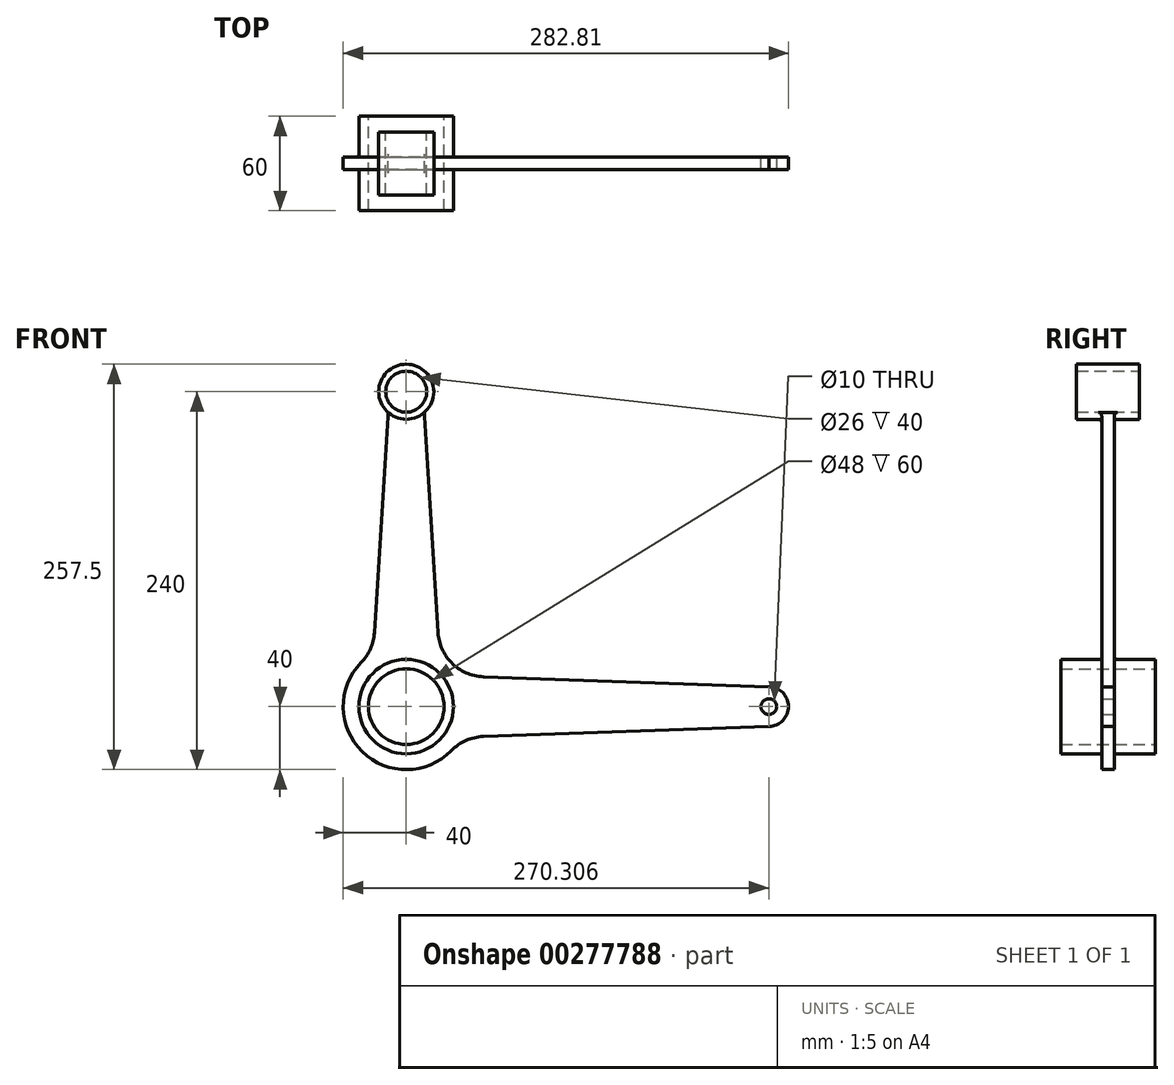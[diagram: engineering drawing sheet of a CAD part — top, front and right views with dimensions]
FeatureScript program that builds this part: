
annotation { "Feature Type Name" : "Feature", "Feature Type Description" : "" }
export const myFeature = defineFeature(function(context is Context, id is Id, definition is map)
    precondition{}
    {
        {
            var Q0;
            Q0=qCreatedBy(makeId("Front.planeOp"),FACE);
            var sketch = newSketch(context, id + "F0", { "sketchPlane" : qUnion([Q0])});
            skCircle(sketch, "E0", {"center": v(0, 0) * mm, "radius": 40 * mm});
            skCircle(sketch, "E1", {"center": v(0, 200) * mm, "radius": 17.5 * mm});
            skLineSegment(sketch, "E2", {"start": v(-11.5, 186.8) * mm, "end": v(-21, 34.04) * mm});
            skLineSegment(sketch, "E3.MirrorCS", {"start": v(11.5, 186.8) * mm, "end": v(21, 34.04) * mm});
            skCircle(sketch, "E4", {"center": v(230.3, 0) * mm, "radius": 12.5 * mm});
            skCircle(sketch, "E5", {"center": v(230.3, 0) * mm, "radius": 5 * mm});
            skLineSegment(sketch, "E6", {"start": v(34.92, 19.5) * mm, "end": v(230.3, 12.5) * mm});
            skLineSegment(sketch, "E7.MirrorCS", {"start": v(34.92, -19.5) * mm, "end": v(230.3, -12.5) * mm});
            skCircle(sketch, "E8", {"center": v(0, 0) * mm, "radius": 30 * mm});
            skCircle(sketch, "E9", {"center": v(0, 0) * mm, "radius": 24 * mm});
            skCircle(sketch, "E10", {"center": v(0, 200) * mm, "radius": 13 * mm});
            skSolve(sketch);
        }
        {
            var Q0;
            Q0 = qSketchRegion(id + "F0", true);
            extrude(context, id + "F1", {"entities" : qUnion([Q0]), "endBound" : BoundingType.SYMMETRIC, "depth" : 8 * mm});
        }
        {
            var Q0;
            Q0=makeQuery(id+"F1.opExtrude","SWEPT_EDGE",EDGE,{"disambiguationData":[OSD([sQuery(id+"F0.wireOp",EDGE,"E0"),sQuery(id+"F0.wireOp",EDGE,"E3.MirrorCS")])]});
            fillet(context, id + "F2", {"entities" : qUnion([Q0]), "radius" : 30 * mm, "tangentPropagation" : true, "allowEdgeOverflow" : false});
        }
        {
            var Q0;
            Q0=makeQuery(id+"F1.opExtrude","SWEPT_EDGE",EDGE,{"disambiguationData":[OSD([sQuery(id+"F0.wireOp",EDGE,"E0"),sQuery(id+"F0.wireOp",EDGE,"E6")])]});
            fillet(context, id + "F3", {"entities" : qUnion([Q0]), "radius" : 30 * mm, "tangentPropagation" : true, "allowEdgeOverflow" : false});
        }
        {
            var Q0;
            Q0=makeQuery(id+"F1.opExtrude","SWEPT_EDGE",EDGE,{"disambiguationData":[OSD([sQuery(id+"F0.wireOp",EDGE,"E0"),sQuery(id+"F0.wireOp",EDGE,"E2")])]});
            fillet(context, id + "F4", {"entities" : qUnion([Q0]), "radius" : 30 * mm, "tangentPropagation" : true, "allowEdgeOverflow" : false});
        }
        {
            var Q0;
            Q0=makeQuery(id+"F1.opExtrude","SWEPT_EDGE",EDGE,{"disambiguationData":[OSD([sQuery(id+"F0.wireOp",EDGE,"E0"),sQuery(id+"F0.wireOp",EDGE,"E7.MirrorCS")])]});
            fillet(context, id + "F5", {"entities" : qUnion([Q0]), "radius" : 30 * mm, "tangentPropagation" : true, "allowEdgeOverflow" : false});
        }
        {
            var Q0;
            Q0=qCreatedBy(makeId("Front.planeOp"),FACE);
            var sketch = newSketch(context, id + "F6", { "sketchPlane" : qUnion([Q0])});
            skCircle(sketch, "E11", {"center": v(0, 0) * mm, "radius": 30 * mm});
            skCircle(sketch, "E12", {"center": v(0, 0) * mm, "radius": 24 * mm});
            skSolve(sketch);
        }
        {
            var Q0;
            Q0=makeQuery(id+"F0.imprint","IMPRINT",FACE,{"disambiguationData":[TD([[makeQuery(id+"F0.imprint","IMPRINT",EDGE,{"derivedFrom":sQuery(id+"F0.wireOp",EDGE,"E10")}),-1.0]])]});
            extrude(context, id + "F7", {"entities" : qUnion([Q0]), "operationType" : NewBodyOperationType.ADD, "endBound" : BoundingType.SYMMETRIC, "depth" : 40 * mm});
        }
        {
            var Q0;
            Q0=makeQuery(id+"F6.imprint","IMPRINT",FACE,{"disambiguationData":[TD([[makeQuery(id+"F6.imprint","IMPRINT",EDGE,{"derivedFrom":sQuery(id+"F6.wireOp",EDGE,"E11")}),1.0]])]});
            extrude(context, id + "F8", {"entities" : qUnion([Q0]), "operationType" : NewBodyOperationType.ADD, "endBound" : BoundingType.SYMMETRIC, "depth" : 60 * mm});
        }
        {
            var Q0;
            Q0=makeQuery(id+"F1.opExtrude","CAP_EDGE",EDGE,{"disambiguationData":[OSD([sQuery(id+"F0.wireOp",EDGE,"E8")])],"isStart":false});
            var Q1;
            Q1=makeQuery(id+"F1.opExtrude","CAP_EDGE",EDGE,{"disambiguationData":[OSD([sQuery(id+"F0.wireOp",EDGE,"E8")])],"isStart":true});
            fillet(context, id + "F9", {"entities" : qUnion([Q0, Q1]), "radius" : 2 * mm, "tangentPropagation" : true, "allowEdgeOverflow" : false});
        }
        {
            var Q0;
            {var subQ0=sQuery(id+"F0.wireOp",EDGE,"E1");Q0=makeQuery(id+"F7.boolean.opBoolean","INTERSECT",EDGE,{"derivedFrom":[makeQuery(id+"F1.opExtrude","CAP_FACE",FACE,{"disambiguationData":[OSD([sQuery(id+"F0.wireOp",EDGE,"E0"),subQ0,sQuery(id+"F0.wireOp",EDGE,"E2"),sQuery(id+"F0.wireOp",EDGE,"E3.MirrorCS"),sQuery(id+"F0.wireOp",EDGE,"E4"),sQuery(id+"F0.wireOp",EDGE,"E5"),sQuery(id+"F0.wireOp",EDGE,"E6"),sQuery(id+"F0.wireOp",EDGE,"E7.MirrorCS"),sQuery(id+"F0.wireOp",EDGE,"E8"),sQuery(id+"F0.wireOp",EDGE,"E10")])],"isStart":false}),makeQuery(id+"F7.opExtrude","SWEPT_FACE",FACE,{"disambiguationData":[OSD([subQ0])]})]});}
            var Q1;
            {var subQ0=sQuery(id+"F0.wireOp",EDGE,"E1");Q1=makeQuery(id+"F7.boolean.opBoolean","INTERSECT",EDGE,{"derivedFrom":[makeQuery(id+"F1.opExtrude","CAP_FACE",FACE,{"disambiguationData":[OSD([sQuery(id+"F0.wireOp",EDGE,"E0"),subQ0,sQuery(id+"F0.wireOp",EDGE,"E2"),sQuery(id+"F0.wireOp",EDGE,"E3.MirrorCS"),sQuery(id+"F0.wireOp",EDGE,"E4"),sQuery(id+"F0.wireOp",EDGE,"E5"),sQuery(id+"F0.wireOp",EDGE,"E6"),sQuery(id+"F0.wireOp",EDGE,"E7.MirrorCS"),sQuery(id+"F0.wireOp",EDGE,"E8"),sQuery(id+"F0.wireOp",EDGE,"E10")])],"isStart":true}),makeQuery(id+"F7.opExtrude","SWEPT_FACE",FACE,{"disambiguationData":[OSD([subQ0])]})]});}
            fillet(context, id + "F10", {"entities" : qUnion([Q0, Q1]), "radius" : 2 * mm, "tangentPropagation" : true, "allowEdgeOverflow" : false});
        }
    });
